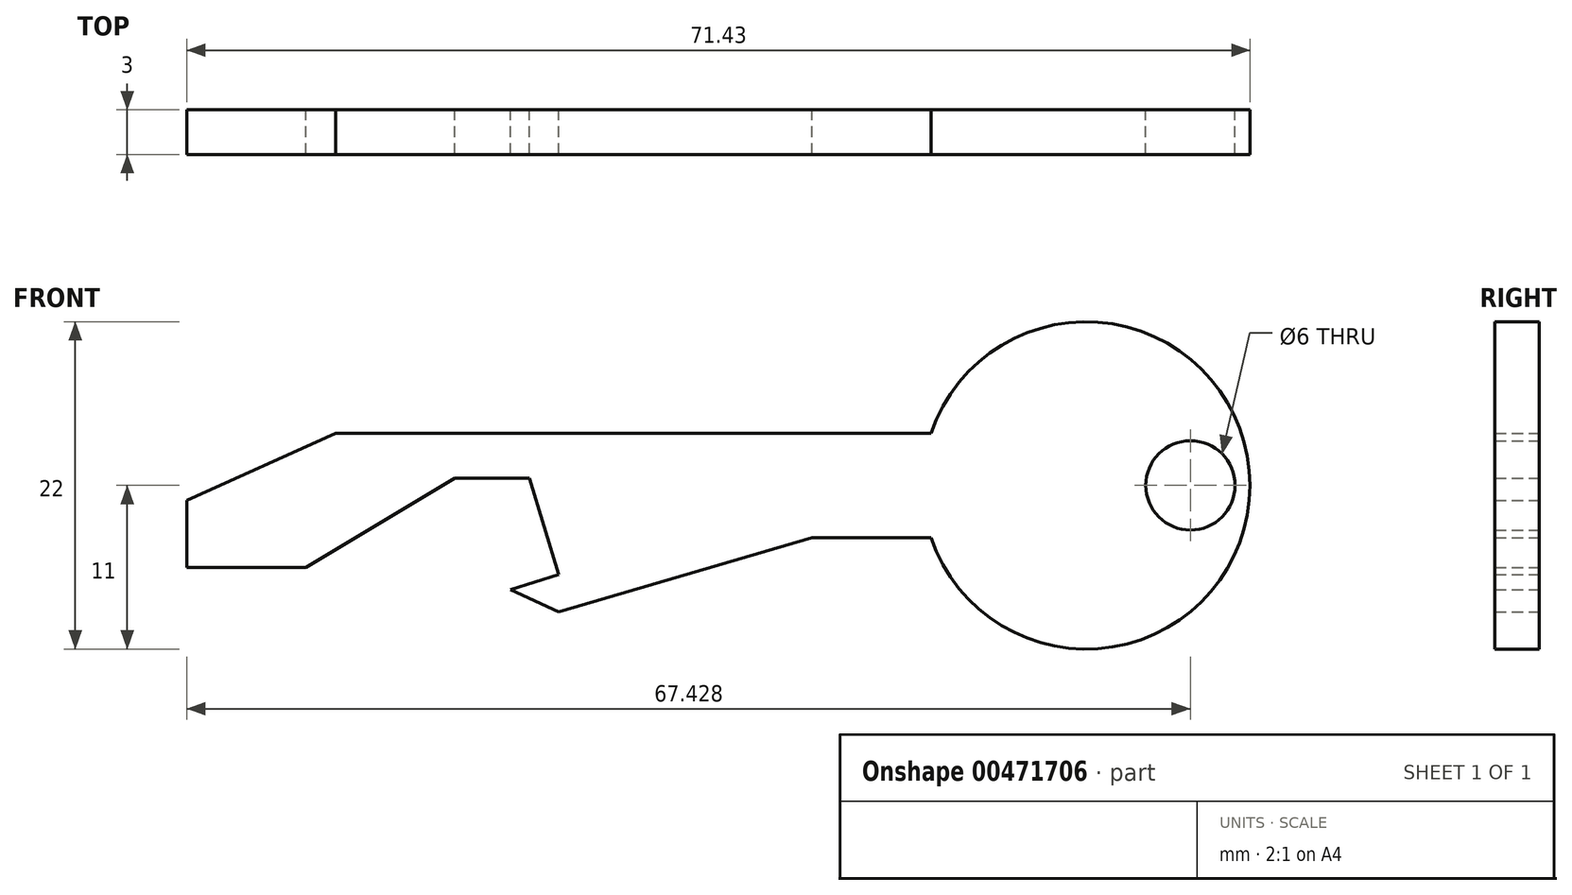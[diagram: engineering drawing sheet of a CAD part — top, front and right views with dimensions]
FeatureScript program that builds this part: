
annotation { "Feature Type Name" : "Feature", "Feature Type Description" : "" }
export const myFeature = defineFeature(function(context is Context, id is Id, definition is map)
    precondition{}
    {
        {
            var Q0;
            Q0=qCreatedBy(makeId("Front.planeOp"),FACE);
            var sketch = newSketch(context, id + "F0", { "sketchPlane" : qUnion([Q0])});
            skLineSegment(sketch, "E0.bottom", {"start": v(0, 0) * mm, "end": v(40, 0) * mm});
            skLineSegment(sketch, "E0.top", {"start": v(0, 7) * mm, "end": v(40, 7) * mm});
            skLineSegment(sketch, "E0.left", {"start": v(0, 0) * mm, "end": v(0, 7) * mm});
            skLineSegment(sketch, "E0.right", {"start": v(40, 0) * mm, "end": v(40, 7) * mm});
            skArc(sketch, "E1", {"start": v(40, 0) * mm, "mid": v(61.43, 3.5) * mm, "end": v(40, 7) * mm});
            skLineSegment(sketch, "E2", {"start": v(0, 7) * mm, "end": v(-10, 2.5) * mm});
            skLineSegment(sketch, "E3", {"start": v(-10, 2.5) * mm, "end": v(-10, -2) * mm});
            skLineSegment(sketch, "E4", {"start": v(-10, -2) * mm, "end": v(-2, -2) * mm});
            skLineSegment(sketch, "E5", {"start": v(-2, -2) * mm, "end": v(8, 4) * mm});
            skLineSegment(sketch, "E6", {"start": v(8, 4) * mm, "end": v(13, 4) * mm});
            skLineSegment(sketch, "E7", {"start": v(13, 4) * mm, "end": v(15, -2.5) * mm});
            skLineSegment(sketch, "E8", {"start": v(15, -2.5) * mm, "end": v(11.75, -3.5) * mm});
            skLineSegment(sketch, "E9", {"start": v(11.75, -3.5) * mm, "end": v(15, -5) * mm});
            skLineSegment(sketch, "E10", {"start": v(15, -5) * mm, "end": v(32, 0) * mm});
            skCircle(sketch, "E11", {"center": v(57.43, 3.5) * mm, "radius": 3 * mm});
            skSolve(sketch);
        }
        {
            var Q0;
            {var subQ0=sQuery(id+"F0.wireOp",EDGE,"E0.left");Q0=makeQuery(id+"F0.imprint","IMPRINT",FACE,{"disambiguationData":[TD([[makeQuery(id+"F0.imprint","IMPRINT",EDGE,{"derivedFrom":subQ0}),1.0]])]});}
            var Q1;
            {var subQ9=sQuery(id+"F0.wireOp",EDGE,"E0.left");Q1=makeQuery(id+"F0.imprint","IMPRINT",FACE,{"disambiguationData":[TD([[makeQuery(id+"F0.imprint","IMPRINT",EDGE,{"derivedFrom":subQ9}),-1.0]])]});}
            var Q2;
            {var subQ4=sQuery(id+"F0.wireOp",EDGE,"E8");Q2=makeQuery(id+"F0.imprint","IMPRINT",FACE,{"disambiguationData":[TD([[makeQuery(id+"F0.imprint","IMPRINT",EDGE,{"derivedFrom":subQ4}),1.0]])]});}
            var Q3;
            {var subQ3=sQuery(id+"F0.wireOp",EDGE,"7VBHRefb-ZezH-LXmD-XGCx-hcoTWlabLQlG");Q3=makeQuery(id+"F0.imprint","IMPRINT",FACE,{"disambiguationData":[TD([[makeQuery(id+"F0.imprint","IMPRINT",EDGE,{"derivedFrom":subQ3}),-1.0]])]});}
            var Q4;
            {var subQ3=sQuery(id+"F0.wireOp",EDGE,"lKG2LDTI-TQmS-NmJ1-liUh-qlYl0mUGQLIu");Q4=makeQuery(id+"F0.imprint","IMPRINT",FACE,{"disambiguationData":[TD([[makeQuery(id+"F0.imprint","IMPRINT",EDGE,{"derivedFrom":subQ3}),-1.0]])]});}
            var Q5;
            {var subQ0=sQuery(id+"F0.wireOp",EDGE,"E0.right");Q5=makeQuery(id+"F0.imprint","IMPRINT",FACE,{"disambiguationData":[TD([[makeQuery(id+"F0.imprint","IMPRINT",EDGE,{"derivedFrom":subQ0}),1.0]])]});}
            var Q6;
            {var subQ0=sQuery(id+"F0.wireOp",EDGE,"E0.right");Q6=makeQuery(id+"F0.imprint","IMPRINT",FACE,{"disambiguationData":[TD([[makeQuery(id+"F0.imprint","IMPRINT",EDGE,{"derivedFrom":subQ0}),-1.0]])]});}
            extrude(context, id + "F1", {"entities" : qUnion([Q0, Q1, Q2, Q3, Q4, Q5, Q6]), "depth" : 3 * mm});
        }
    });
